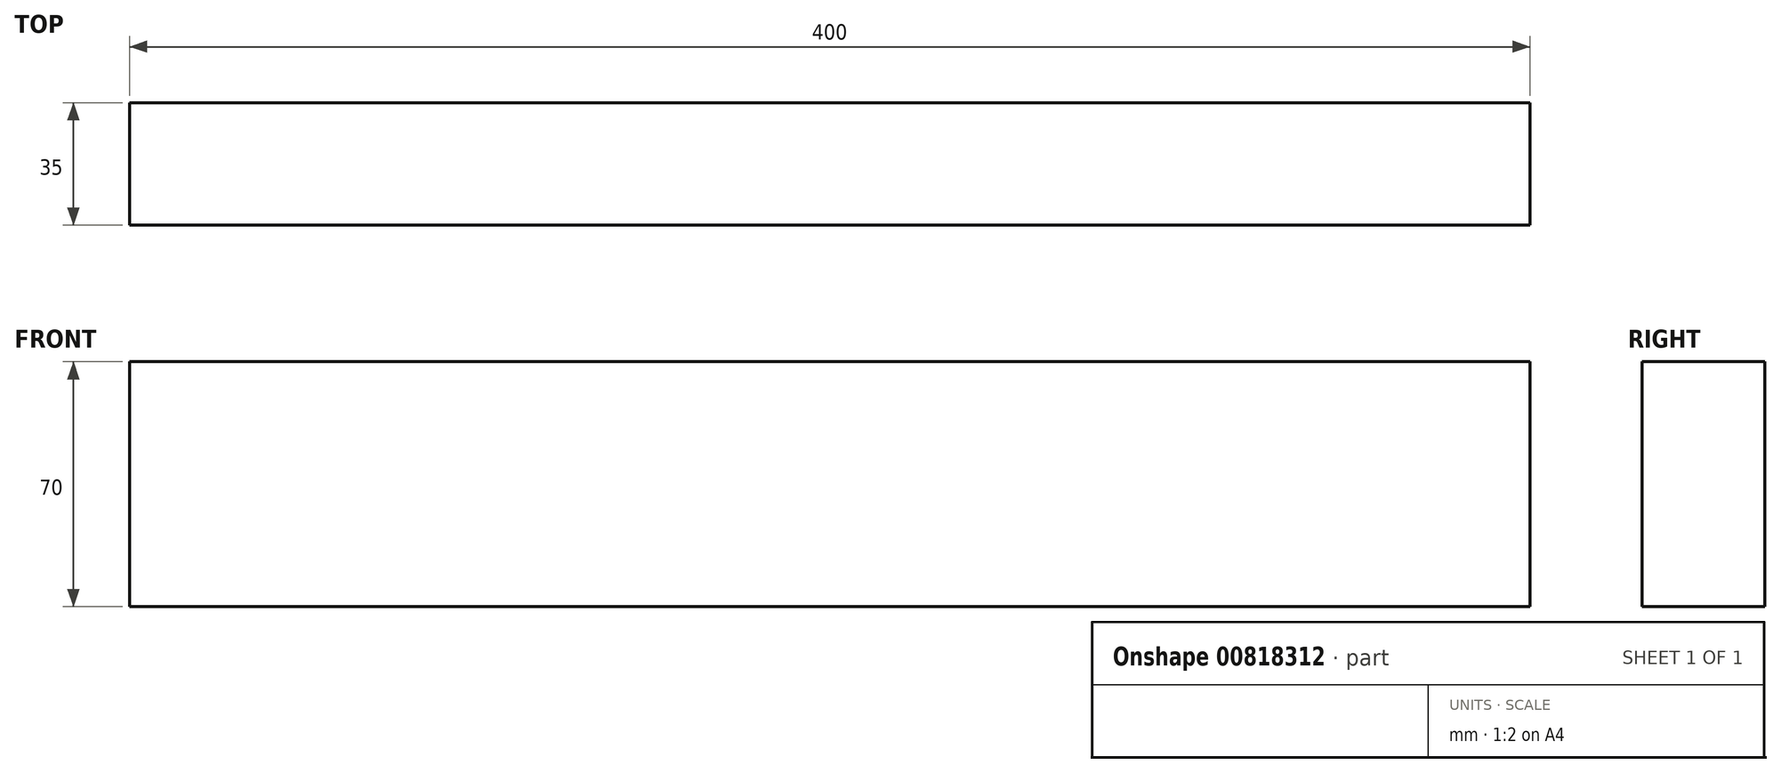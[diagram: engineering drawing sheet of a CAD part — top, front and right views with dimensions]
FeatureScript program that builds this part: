
annotation { "Feature Type Name" : "Feature", "Feature Type Description" : "" }
export const myFeature = defineFeature(function(context is Context, id is Id, definition is map)
    precondition{}
    {
        {
            var Q0;
            Q0=qCreatedBy(makeId("Front.planeOp"),FACE);
            var sketch = newSketch(context, id + "F0", { "sketchPlane" : qUnion([Q0])});
            skLineSegment(sketch, "E0.bottom", {"start": v(0, 0) * mm, "end": v(400, 0) * mm});
            skLineSegment(sketch, "E0.top", {"start": v(0, -70) * mm, "end": v(400, -70) * mm});
            skLineSegment(sketch, "E0.left", {"start": v(0, 0) * mm, "end": v(0, -70) * mm});
            skLineSegment(sketch, "E0.right", {"start": v(400, 0) * mm, "end": v(400, -70) * mm});
            skSolve(sketch);
        }
        {
            var Q0;
            Q0 = qSketchRegion(id + "F0", true);
            extrude(context, id + "F1", {"entities" : qUnion([Q0]), "depth" : 35 * mm, "offsetDistance" : 25 * mm});
        }
    });
